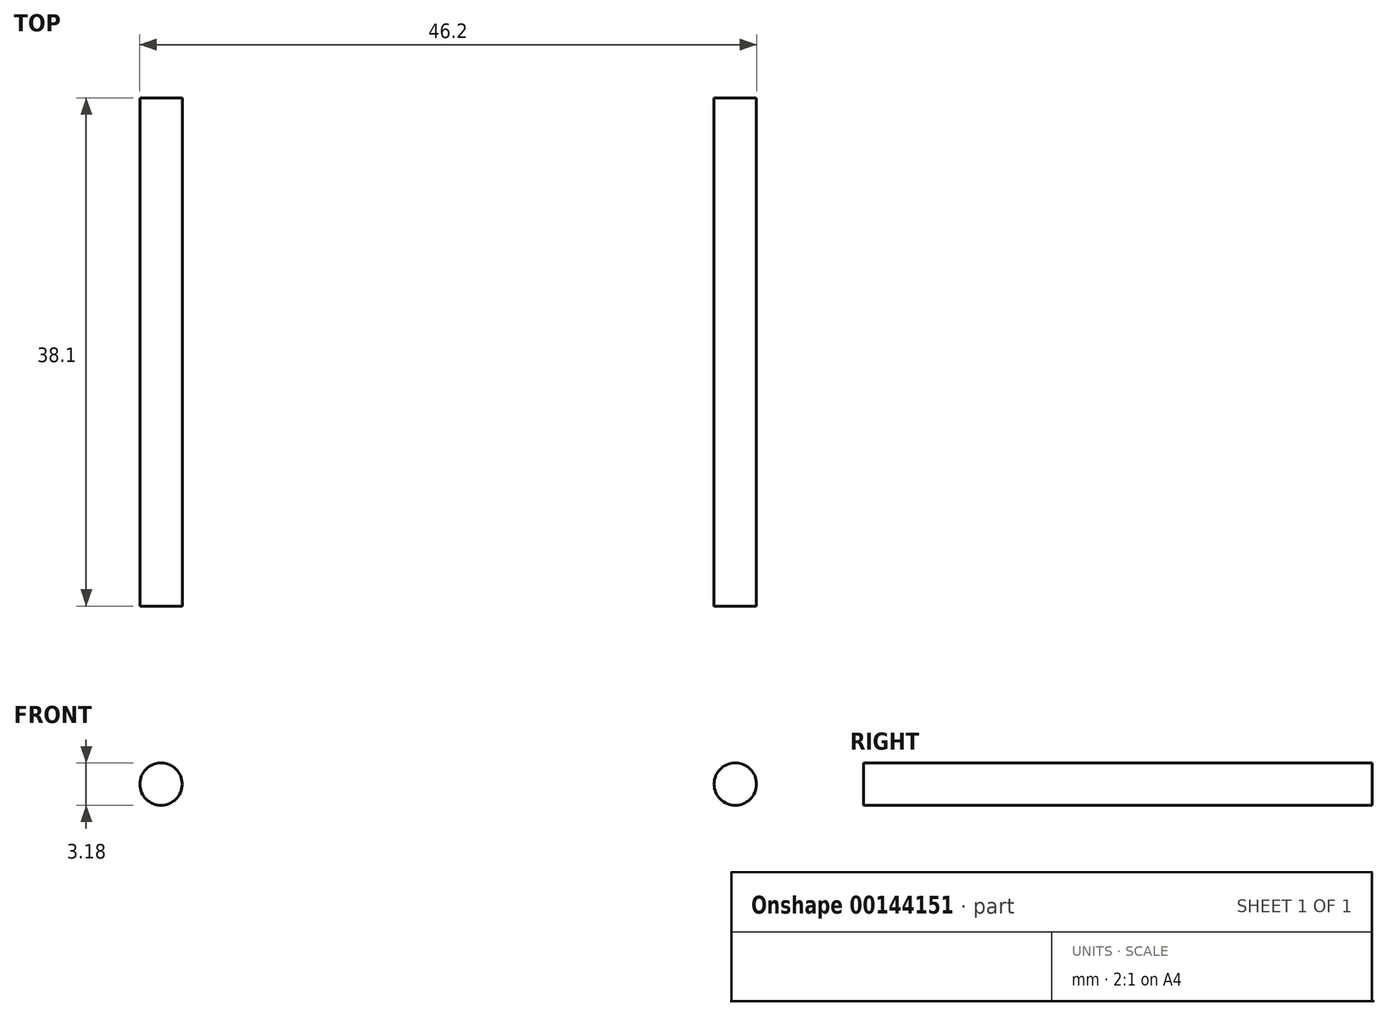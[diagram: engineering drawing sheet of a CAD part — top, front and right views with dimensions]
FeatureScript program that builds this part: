
annotation { "Feature Type Name" : "Feature", "Feature Type Description" : "" }
export const myFeature = defineFeature(function(context is Context, id is Id, definition is map)
    precondition{}
    {
        {
            var Q0;
            Q0=qCreatedBy(makeId("Front.planeOp"),FACE);
            var sketch = newSketch(context, id + "F0", { "sketchPlane" : qUnion([Q0])});
            skCircle(sketch, "E0", {"center": v(-24.17, 0) * mm, "radius": 1.59 * mm});
            skCircle(sketch, "E1", {"center": v(18.85, 0) * mm, "radius": 1.59 * mm});
            skSolve(sketch);
        }
        {
            var Q0;
            Q0=qSketchRegion(id+"F0",true);
            extrude(context, id + "F1", {"entities" : qUnion([Q0]), "depth" : 38.1 * mm});
        }
    });
